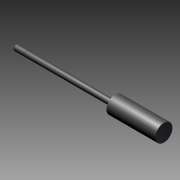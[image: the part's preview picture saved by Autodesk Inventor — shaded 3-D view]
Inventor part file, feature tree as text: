
AUTODESK INVENTOR PART (.ipt)
format: ipt  version: 2012 (Build 160160000, 160)  size: 124,416 bytes
history: native  units: in
note: dims shown in document units (in); Inventor stores cm internally (conversion verified against a paired STEP export)
features: other x70, revolve x3, sketch x3
ambient origin geometry x8: Origin, YZ Plane, XZ Plane, XY Plane, X Axis, Y Axis, Z Axis, Center Point
bodies: Solid1 (feature_tree)
feature tree (76):
  revolve  "Revolution1"  Angle=360.0deg
  revolve  "Revolution2"  [1 undecoded]
  revolve  "Revolution3"  [1 undecoded]
  other  "rod_cp_XY"
  other  "rod_cp_YZ"
  other  "rod_cp_ZX"
  other  "rod_cp_X"
  other  "rod_cp_Y"
  other  "rod_cp_Z"
  other  "rod_cp_Center"
  other  "to_rod_clevis_XY"
  other  "to_rod_clevis_YZ"
  other  "to_rod_clevis_ZX"
  other  "to_rod_clevis_X"
  other  "to_rod_clevis_Y"
  other  "to_rod_clevis_Z"
  other  "to_rod_clevis_Center"
  other  "rl2_XY"
  other  "rl2_YZ"
  other  "rl2_ZX"
  other  "rl2_X"
  other  "rl2_Y"
  other  "rl2_Z"
  other  "rl2_Center"
  other  "rl1_XY"
  other  "rl1_YZ"
  other  "rl1_ZX"
  other  "rl1_X"
  other  "rl1_Y"
  other  "rl1_Z"
  other  "rl1_Center"
  other  "thd1_XY"
  other  "thd1_YZ"
  other  "thd1_ZX"
  other  "thd1_X"
  other  "thd1_Y"
  other  "thd1_Z"
  other  "thd1_Center"
  other  "thd2_XY"
  other  "thd2_YZ"
  other  "thd2_ZX"
  other  "thd2_X"
  other  "thd2_Y"
  other  "thd2_Z"
  other  "thd2_Center"
  other  "dia1_XY"
  other  "dia1_YZ"
  other  "dia1_ZX"
  other  "dia1_X"
  other  "dia1_Y"
  other  "dia1_Z"
  other  "dia1_Center"
  other  "dia2_XY"
  other  "dia2_YZ"
  other  "dia2_ZX"
  other  "dia2_X"
  other  "dia2_Y"
  other  "dia2_Z"
  other  "dia2_Center"
  other  "dia12_XY"
  other  "dia12_YZ"
  other  "dia12_ZX"
  other  "dia12_X"
  other  "dia12_Y"
  other  "dia12_Z"
  other  "dia12_Center"
  other  "dia22_XY"
  other  "dia22_YZ"
  other  "dia22_ZX"
  other  "dia22_X"
  other  "dia22_Y"
  other  "dia22_Z"
  other  "dia22_Center"
  sketch  "Sketch_1"  dims[d0=360.0deg d1=360.0deg]
  sketch  "Sketch_3"  dims[d2=360.0deg]
  sketch  "Sketch_30"
note: 2 required parameter values undecoded (feature->parameter linkage not recoverable at this tier; creation-order binding heuristic only, values carry confidence <= 0.55)
